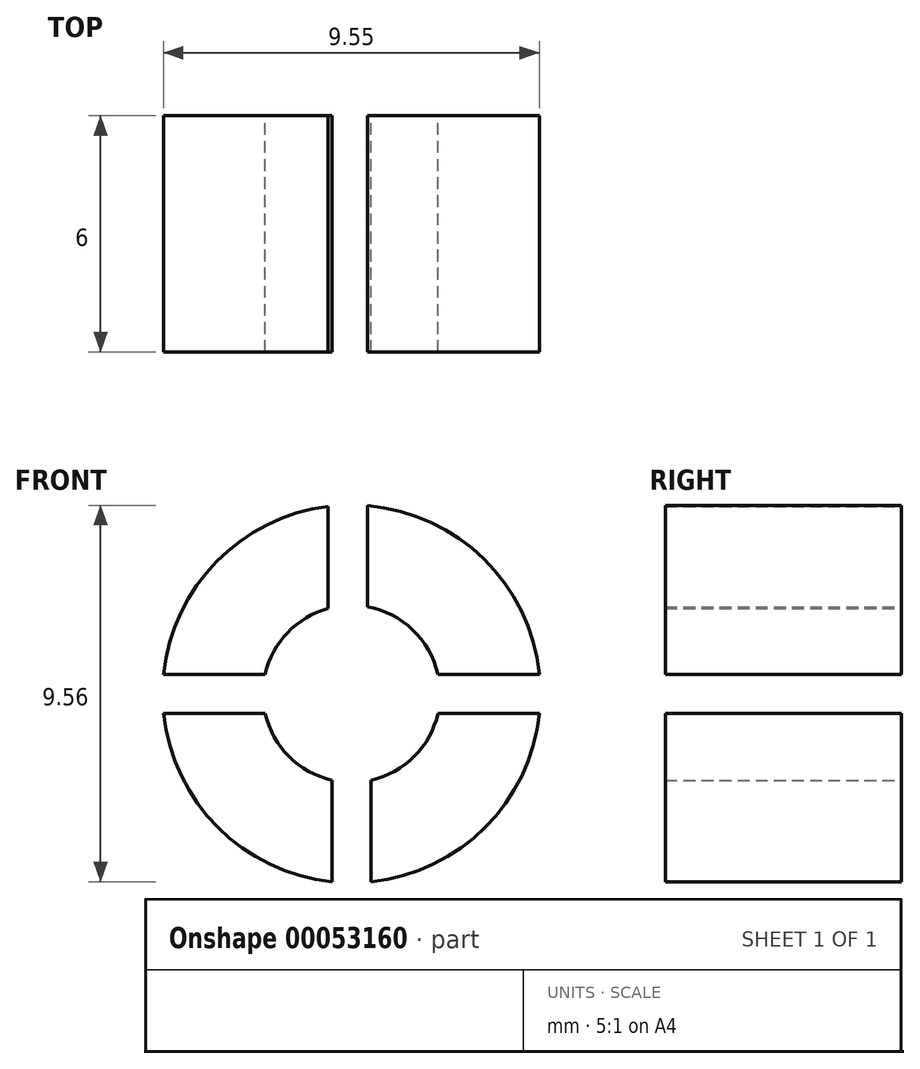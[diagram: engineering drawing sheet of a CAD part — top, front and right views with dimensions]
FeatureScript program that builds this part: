
annotation { "Feature Type Name" : "Feature", "Feature Type Description" : "" }
export const myFeature = defineFeature(function(context is Context, id is Id, definition is map)
    precondition{}
    {
        {
            var Q0;
            Q0=qCreatedBy(makeId("Front.planeOp"),FACE);
            var sketch = newSketch(context, id + "F0", { "sketchPlane" : qUnion([Q0])});
            skCircle(sketch, "E0", {"center": v(-22.53, 19.75) * mm, "radius": 4.8 * mm});
            skCircle(sketch, "E1", {"center": v(-22.53, 19.75) * mm, "radius": 2.25 * mm});
            skLineSegment(sketch, "E2", {"start": v(-23.03, 17.56) * mm, "end": v(-23.03, 14.98) * mm});
            skLineSegment(sketch, "E3", {"start": v(-23.03, 14.98) * mm, "end": v(-22.03, 14.98) * mm});
            skLineSegment(sketch, "E4", {"start": v(-22.03, 14.98) * mm, "end": v(-22.03, 17.56) * mm});
            skLineSegment(sketch, "E5", {"start": v(-20.34, 20.25) * mm, "end": v(-17.76, 20.25) * mm});
            skLineSegment(sketch, "E6", {"start": v(-17.76, 20.25) * mm, "end": v(-17.76, 19.25) * mm});
            skLineSegment(sketch, "E7", {"start": v(-17.76, 19.25) * mm, "end": v(-20.34, 19.25) * mm});
            skLineSegment(sketch, "E8", {"start": v(-20.34, 19.25) * mm, "end": v(-17.76, 19.25) * mm});
            skLineSegment(sketch, "E9", {"start": v(-23.13, 24.51) * mm, "end": v(-23.13, 21.92) * mm});
            skLineSegment(sketch, "E10", {"start": v(-23.13, 21.92) * mm, "end": v(-22.13, 21.97) * mm});
            skLineSegment(sketch, "E11", {"start": v(-22.13, 21.97) * mm, "end": v(-22.13, 24.54) * mm});
            skLineSegment(sketch, "E12", {"start": v(-27.3, 20.25) * mm, "end": v(-24.73, 20.25) * mm});
            skLineSegment(sketch, "E13", {"start": v(-24.73, 20.25) * mm, "end": v(-24.73, 19.25) * mm});
            skLineSegment(sketch, "E14", {"start": v(-24.73, 19.25) * mm, "end": v(-27.3, 19.25) * mm});
            skSolve(sketch);
        }
        {
            var Q0;
            {var subQ0=sQuery(id+"F0.wireOp",EDGE,"E9");Q0=makeQuery(id+"F0.imprint","IMPRINT",FACE,{"disambiguationData":[TD([[makeQuery(id+"F0.imprint","IMPRINT",EDGE,{"derivedFrom":subQ0}),-1.0]])]});}
            var Q1;
            {var subQ0=sQuery(id+"F0.wireOp",EDGE,"E5");Q1=makeQuery(id+"F0.imprint","IMPRINT",FACE,{"disambiguationData":[TD([[makeQuery(id+"F0.imprint","IMPRINT",EDGE,{"derivedFrom":subQ0}),1.0]])]});}
            var Q2;
            {var subQ0=sQuery(id+"F0.wireOp",EDGE,"E4");Q2=makeQuery(id+"F0.imprint","IMPRINT",FACE,{"disambiguationData":[TD([[makeQuery(id+"F0.imprint","IMPRINT",EDGE,{"derivedFrom":subQ0}),-1.0]])]});}
            var Q3;
            {var subQ0=sQuery(id+"F0.wireOp",EDGE,"E2");Q3=makeQuery(id+"F0.imprint","IMPRINT",FACE,{"disambiguationData":[TD([[makeQuery(id+"F0.imprint","IMPRINT",EDGE,{"derivedFrom":subQ0}),-1.0]])]});}
            extrude(context, id + "F1", {"entities" : qUnion([Q0, Q1, Q2, Q3]), "depth" : 6 * mm});
        }
    });
